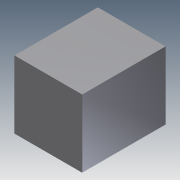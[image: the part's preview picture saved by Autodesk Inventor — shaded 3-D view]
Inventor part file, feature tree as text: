
AUTODESK INVENTOR PART (.ipt)
format: ipt  version: 2011 (Build 150239000, 239)  size: 69,120 bytes
history: native  units: in
note: dims shown in document units (in); Inventor stores cm internally (conversion verified against a paired STEP export)
features: extrude x1, sketch x1
ambient origin geometry x8: Origin, YZ Plane, XZ Plane, XY Plane, X Axis, Y Axis, Z Axis, Center Point
bodies: Solid1 (feature_tree)
feature tree (2):
  extrude  "Extrusion1"  Depth=1.6in
  sketch  "Sketch1"  dims[d0=1.6in d1=1.6in d2=1.97in d3=0.0in]
